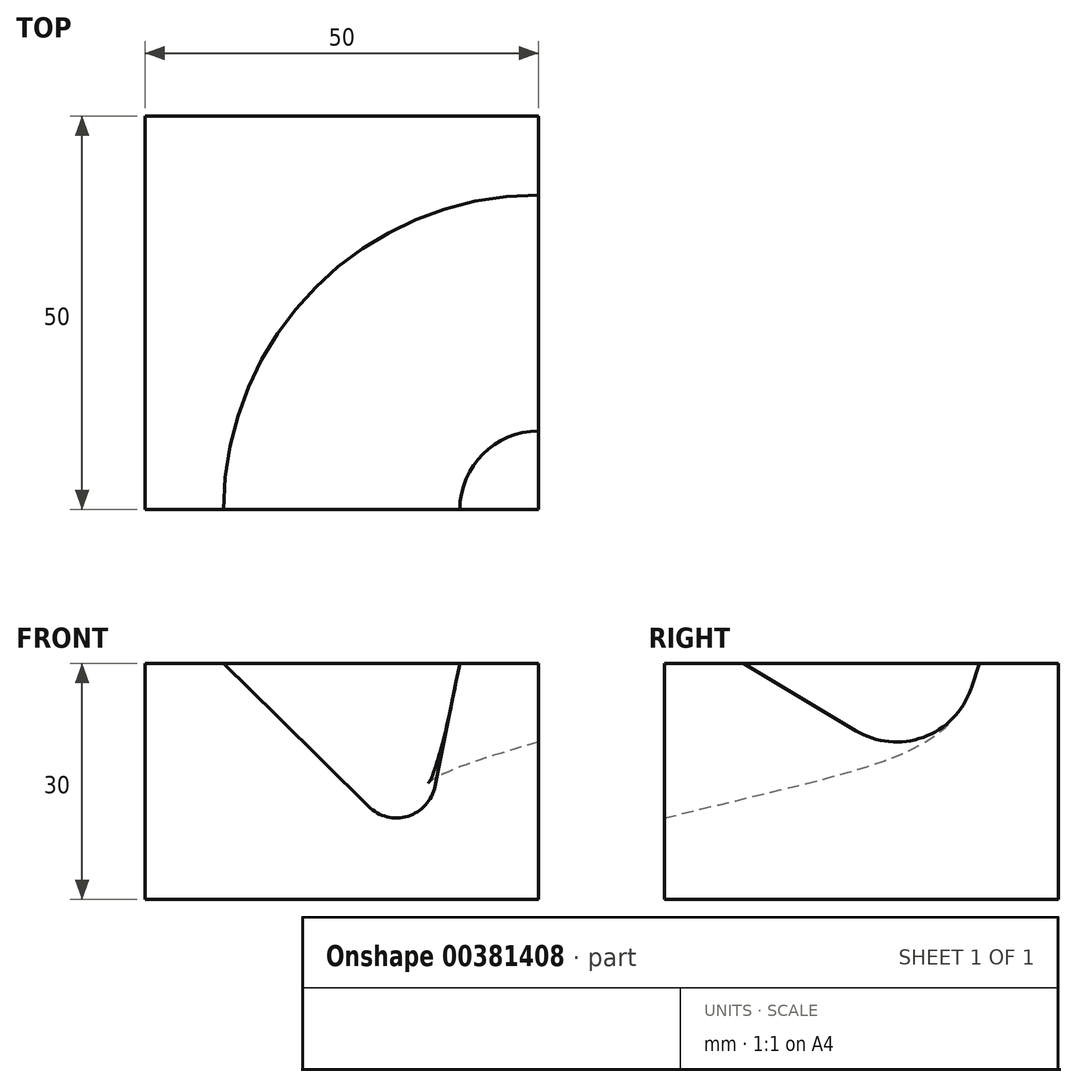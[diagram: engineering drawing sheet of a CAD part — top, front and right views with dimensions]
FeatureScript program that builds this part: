
annotation { "Feature Type Name" : "Feature", "Feature Type Description" : "" }
export const myFeature = defineFeature(function(context is Context, id is Id, definition is map)
    precondition{}
    {
        {
            var Q0;
            Q0=qCreatedBy(makeId("Front.planeOp"),FACE);
            var sketch = newSketch(context, id + "F0", { "sketchPlane" : qUnion([Q0])});
            skLineSegment(sketch, "E0.bottom", {"start": v(0, 0) * mm, "end": v(-50, 0) * mm});
            skLineSegment(sketch, "E0.top", {"start": v(0, 30) * mm, "end": v(-50, 30) * mm});
            skLineSegment(sketch, "E0.left", {"start": v(0, 0) * mm, "end": v(0, 30) * mm});
            skLineSegment(sketch, "E0.right", {"start": v(-50, 0) * mm, "end": v(-50, 30) * mm});
            skSolve(sketch);
        }
        {
            var Q0;
            Q0=makeQuery(id+"F0.imprint","IMPRINT",FACE,{"disambiguationData":[TD([[makeQuery(id+"F0.imprint","IMPRINT",EDGE,{"derivedFrom":sQuery(id+"F0.wireOp",EDGE,"E0.bottom")}),-1.0]])]});
            extrude(context, id + "F1", {"entities" : qUnion([Q0]), "oppositeDirection" : true, "depth" : 50 * mm});
        }
        {
            var Q0;
            Q0=makeQuery(id+"F1.opExtrude","CAP_FACE",FACE,{"disambiguationData":[OSD([sQuery(id+"F0.wireOp",EDGE,"E0.bottom"),sQuery(id+"F0.wireOp",EDGE,"E0.top"),sQuery(id+"F0.wireOp",EDGE,"E0.left"),sQuery(id+"F0.wireOp",EDGE,"E0.right")])],"isStart":true});
            var sketch = newSketch(context, id + "F2", { "sketchPlane" : qUnion([Q0])});
            skLineSegment(sketch, "E1", {"start": v(-40, 30) * mm, "end": v(-21.58, 11.79) * mm});
            skArc(sketch, "E2", {"start": v(-21.58, 11.79) * mm, "mid": v(-16.6, 10.56) * mm, "end": v(-13.17, 14.35) * mm});
            skLineSegment(sketch, "E3", {"start": v(-10, 30) * mm, "end": v(-13.17, 14.35) * mm});
            skLineSegment(sketch, "E4", {"start": v(-21.58, 11.79) * mm, "end": v(-15, 5.28) * mm, "construction": true});
            skLineSegment(sketch, "E5", {"start": v(-13.17, 14.35) * mm, "end": v(-15, 5.28) * mm, "construction": true});
            skSolve(sketch);
        }
        {
            var Q0;
            Q0=makeQuery(id+"F1.opExtrude","SWEPT_FACE",FACE,{"disambiguationData":[OSD([sQuery(id+"F0.wireOp",EDGE,"E0.top")])]});
            var sketch = newSketch(context, id + "F3", { "sketchPlane" : qUnion([Q0])});
            skArc(sketch, "E6", {"start": v(-10, 0) * mm, "mid": v(-7.07, 7.07) * mm, "end": v(0, 10) * mm});
            skArc(sketch, "E7", {"start": v(-40, 0) * mm, "mid": v(-28.28, 28.28) * mm, "end": v(0, 40) * mm});
            skSolve(sketch);
        }
        {
            var Q0;
            Q0=makeQuery(id+"F1.opExtrude","SWEPT_FACE",FACE,{"disambiguationData":[OSD([sQuery(id+"F0.wireOp",EDGE,"E0.left")])]});
            var sketch = newSketch(context, id + "F4", { "sketchPlane" : qUnion([Q0])});
            skLineSegment(sketch, "E8", {"start": v(10, 30) * mm, "end": v(24.31, 21.41) * mm});
            skArc(sketch, "E9", {"start": v(24.31, 21.41) * mm, "mid": v(32.92, 20.6) * mm, "end": v(38.94, 26.83) * mm});
            skLineSegment(sketch, "E10", {"start": v(38.94, 26.83) * mm, "end": v(40, 30) * mm});
            skLineSegment(sketch, "E11", {"start": v(38.94, 26.83) * mm, "end": v(35, 15) * mm, "construction": true});
            skLineSegment(sketch, "E12", {"start": v(24.31, 21.41) * mm, "end": v(35, 15) * mm, "construction": true});
            skSolve(sketch);
        }
        {
            var Q1;
            {var subQ0=sQuery(id+"F2.wireOp",EDGE,"E1");Q1=makeQuery(id+"F2.imprint","IMPRINT",FACE,{"disambiguationData":[TD([[makeQuery(id+"F2.imprint","IMPRINT",EDGE,{"derivedFrom":subQ0}),1.0]])]});}
            var Q2;
            {var subQ0=sQuery(id+"F4.wireOp",EDGE,"E8");Q2=makeQuery(id+"F4.imprint","IMPRINT",FACE,{"disambiguationData":[TD([[makeQuery(id+"F4.imprint","IMPRINT",EDGE,{"derivedFrom":subQ0}),1.0]])]});}
            var Q3;
            Q3=sQuery(id+"F3.wireOp",EDGE,"E7");
            var Q4;
            Q4=sQuery(id+"F3.wireOp",EDGE,"E6");
            loft(context, id + "F5", {"operationType" : NewBodyOperationType.REMOVE, "addGuides" : true, "sheetProfilesArray" : [{ "sheetProfileEntities" : qUnion([Q1]) }, { "sheetProfileEntities" : qUnion([Q2]) }], "guidesArray" : [{ "guideEntities" : qUnion([Q3]), "guideDerivativeType" : LoftGuideDerivativeType.DEFAULT, "guideDerivativeMagnitude" : 1 }, { "guideEntities" : qUnion([Q4]), "guideDerivativeType" : LoftGuideDerivativeType.DEFAULT, "guideDerivativeMagnitude" : 1 }]});
        }
    });
